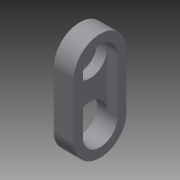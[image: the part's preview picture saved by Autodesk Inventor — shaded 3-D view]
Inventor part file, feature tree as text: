
AUTODESK INVENTOR PART (.ipt)
format: ipt  version: 2015 (Build 190159000, 159)  size: 104,960 bytes
history: native  units: mm
features: extrude x2, sketch x2
ambient origin geometry x8: Origin, YZ Plane, XZ Plane, XY Plane, X Axis, Y Axis, Z Axis, Center Point
bodies: Solid1 (feature_tree)
feature tree (4):
  extrude  "Extrusion1"  Depth=17.0mm
  extrude  "Extrusion2"  Depth=26.0mm
  sketch  "Sketch1"  dims[d12=17.0mm d13=17.0mm]
  sketch  "Sketch2"  dims[d15=26.0mm d16=26.0mm d17=10.0mm d18=0.0mm d19=90.0deg d20=90.0deg d21=5.0mm d22=0.0mm]
